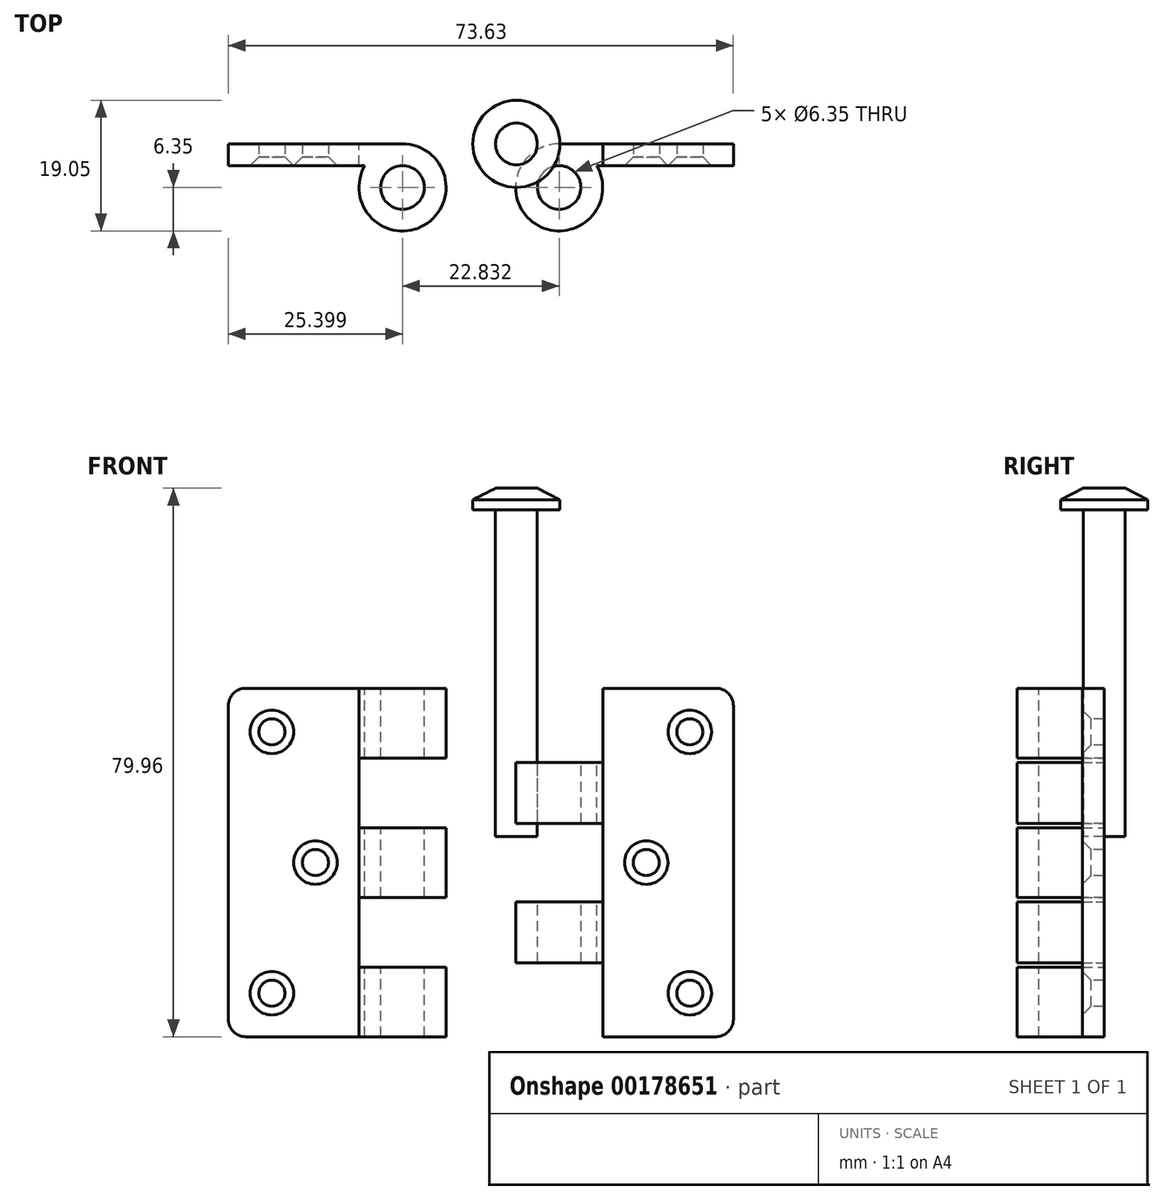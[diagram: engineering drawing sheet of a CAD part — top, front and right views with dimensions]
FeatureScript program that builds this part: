
annotation { "Feature Type Name" : "Feature", "Feature Type Description" : "" }
export const myFeature = defineFeature(function(context is Context, id is Id, definition is map)
    precondition{}
    {
        {
            var Q0;
            Q0=qCreatedBy(makeId("Front.planeOp"),FACE);
            var sketch = newSketch(context, id + "F0", { "sketchPlane" : qUnion([Q0])});
            skLineSegment(sketch, "E0.bottom", {"start": v(-44.61, 38.03) * mm, "end": v(-19.21, 38.03) * mm});
            skLineSegment(sketch, "E0.top", {"start": v(-44.61, -12.77) * mm, "end": v(-19.21, -12.77) * mm});
            skLineSegment(sketch, "E0.left", {"start": v(-44.61, 38.03) * mm, "end": v(-44.61, -12.77) * mm});
            skLineSegment(sketch, "E0.right", {"start": v(-19.21, 38.03) * mm, "end": v(-19.21, -12.77) * mm});
            skSolve(sketch);
        }
        {
            var Q0;
            Q0=qSketchRegion(id+"F0",true);
            extrude(context, id + "F1", {"entities" : qUnion([Q0]), "depth" : 3.17 * mm});
        }
        {
            var Q0;
            Q0=makeQuery(id+"F1.opExtrude","SWEPT_FACE",FACE,{"disambiguationData":[OSD([sQuery(id+"F0.wireOp",EDGE,"E0.bottom")])]});
            var sketch = newSketch(context, id + "F2", { "sketchPlane" : qUnion([Q0])});
            skCircle(sketch, "E1", {"center": v(-19.21, -6.35) * mm, "radius": 6.35 * mm});
            skCircle(sketch, "E2", {"center": v(-19.21, -6.35) * mm, "radius": 3.18 * mm});
            skSolve(sketch);
        }
        {
            var Q0;
            {var subQ5=sQuery(id+"F2.wireOp",EDGE,"E2");Q0=makeQuery(id+"F2.imprint","IMPRINT",FACE,{"disambiguationData":[TD([[makeQuery(id+"F2.imprint","IMPRINT",EDGE,{"derivedFrom":subQ5}),-1.0]])]});}
            var Q1;
            {var subQ1=sQuery(id+"F0.wireOp",EDGE,"E0.bottom");var subQ2=makeQuery(id+"F1.opExtrude","SWEPT_EDGE",EDGE,{"disambiguationData":[OSD([subQ1,sQuery(id+"F0.wireOp",EDGE,"E0.right")])]});Q1=makeQuery(id+"F2.imprint","IMPRINT",FACE,{"disambiguationData":[TD([[makeQuery(id+"F2.imprint","IMPRINT",EDGE,{"derivedFrom":subQ2}),1.0]])]});}
            var Q2;
            Q2=makeQuery(id+"F1.opExtrude","SWEPT_FACE",FACE,{"disambiguationData":[OSD([sQuery(id+"F0.wireOp",EDGE,"E0.top")])]});
            extrude(context, id + "F3", {"entities" : qUnion([Q0, Q1]), "operationType" : NewBodyOperationType.ADD, "endBound" : BoundingType.UP_TO_SURFACE, "oppositeDirection" : true, "endBoundEntityFace" : qUnion([Q2]), "depth" : 25.4 * mm});
        }
        {
            var Q0;
            Q0=makeQuery(id+"F1.opExtrude","CAP_FACE",FACE,{"disambiguationData":[OSD([sQuery(id+"F0.wireOp",EDGE,"E0.bottom"),sQuery(id+"F0.wireOp",EDGE,"E0.top"),sQuery(id+"F0.wireOp",EDGE,"E0.left"),sQuery(id+"F0.wireOp",EDGE,"E0.right")])],"isStart":false});
            var sketch = newSketch(context, id + "F4", { "sketchPlane" : qUnion([Q0])});
            skLineSegment(sketch, "E3", {"start": v(-34.66, 38.03) * mm, "end": v(-34.66, -12.77) * mm, "construction": true});
            skLineSegment(sketch, "E4", {"start": v(-24.7, 12.63) * mm, "end": v(-44.61, 12.63) * mm, "construction": true});
            skLineSegment(sketch, "E5", {"start": v(-24.7, -6.42) * mm, "end": v(-44.61, -6.42) * mm, "construction": true});
            skLineSegment(sketch, "E6", {"start": v(-24.7, 31.68) * mm, "end": v(-44.61, 31.68) * mm, "construction": true});
            skPoint(sketch, "E7", {"position": v(-38.26, 31.68) * mm});
            skPoint(sketch, "E8", {"position": v(-31.91, 12.63) * mm});
            skPoint(sketch, "E9", {"position": v(-38.26, -6.42) * mm});
            skSolve(sketch);
        }
        {
            var Q0;
            Q0=makeQuery(id+"F1.opExtrude","SWEPT_EDGE",EDGE,{"disambiguationData":[OSD([sQuery(id+"F0.wireOp",EDGE,"E0.bottom"),sQuery(id+"F0.wireOp",EDGE,"E0.left")])]});
            var Q1;
            Q1=makeQuery(id+"F1.opExtrude","SWEPT_EDGE",EDGE,{"disambiguationData":[OSD([sQuery(id+"F0.wireOp",EDGE,"E0.top"),sQuery(id+"F0.wireOp",EDGE,"E0.left")])]});
            fillet(context, id + "F5", {"entities" : qUnion([Q0, Q1]), "radius" : 2.54 * mm, "tangentPropagation" : true, "allowEdgeOverflow" : false});
        }
        {
            var Q0;
            Q0=makeQuery(id+"F0.imprint","IMPRINT",FACE,{"disambiguationData":[TD([[makeQuery(id+"F0.imprint","IMPRINT",EDGE,{"derivedFrom":sQuery(id+"F0.wireOp",EDGE,"E0.bottom")}),-1.0]])]});
            var sketch = newSketch(context, id + "F6", { "sketchPlane" : qUnion([Q0])});
            skLineSegment(sketch, "E10", {"start": v(-25.56, -2.61) * mm, "end": v(-12.86, -2.61) * mm});
            skLineSegment(sketch, "E11", {"start": v(-12.86, -2.61) * mm, "end": v(-12.86, 7.55) * mm});
            skLineSegment(sketch, "E12", {"start": v(-12.86, 7.55) * mm, "end": v(-25.56, 7.55) * mm});
            skLineSegment(sketch, "E13", {"start": v(-25.56, 7.55) * mm, "end": v(-25.56, -2.61) * mm});
            skLineSegment(sketch, "E14", {"start": v(-25.56, 17.7) * mm, "end": v(-12.86, 17.7) * mm});
            skLineSegment(sketch, "E15", {"start": v(-12.86, 17.7) * mm, "end": v(-12.86, 27.87) * mm});
            skLineSegment(sketch, "E16", {"start": v(-12.86, 27.87) * mm, "end": v(-25.56, 27.87) * mm});
            skLineSegment(sketch, "E17", {"start": v(-25.56, 27.87) * mm, "end": v(-25.56, 17.7) * mm});
            skPoint(sketch, "E18", {"position": v(-19.21, -2.61) * mm});
            skLineSegment(sketch, "E19", {"start": v(-19.21, 27.87) * mm, "end": v(-19.21, 38.03) * mm});
            skLineSegment(sketch, "E20", {"start": v(-19.21, 17.7) * mm, "end": v(-19.21, 7.55) * mm});
            skLineSegment(sketch, "E21", {"start": v(-19.21, -2.61) * mm, "end": v(-19.21, -12.77) * mm});
            skLineSegment(sketch, "E22", {"start": v(-12.86, 17.7) * mm, "end": v(-12.86, 7.55) * mm});
            skLineSegment(sketch, "E23", {"start": v(-25.56, 7.55) * mm, "end": v(-25.56, 17.7) * mm});
            skLineSegment(sketch, "E24", {"start": v(-25.56, 27.87) * mm, "end": v(-25.56, 38.04) * mm});
            skLineSegment(sketch, "E25", {"start": v(-25.56, 38.04) * mm, "end": v(-12.86, 38.03) * mm});
            skLineSegment(sketch, "E26", {"start": v(-12.86, 38.03) * mm, "end": v(-12.86, 27.87) * mm});
            skLineSegment(sketch, "E27", {"start": v(-12.86, -2.61) * mm, "end": v(-12.86, -12.77) * mm});
            skLineSegment(sketch, "E28", {"start": v(-12.86, -12.77) * mm, "end": v(-25.56, -12.77) * mm});
            skLineSegment(sketch, "E29", {"start": v(-25.56, -12.77) * mm, "end": v(-25.56, -2.61) * mm});
            skSolve(sketch);
        }
        {
            var Q0;
            {var subQ0=sQuery(id+"F6.wireOp",EDGE,"E17");Q0=makeQuery(id+"F6.imprint","IMPRINT",FACE,{"disambiguationData":[TD([[makeQuery(id+"F6.imprint","IMPRINT",EDGE,{"derivedFrom":subQ0}),1.0]])]});}
            var Q1;
            {var subQ0=sQuery(id+"F6.wireOp",EDGE,"E15");Q1=makeQuery(id+"F6.imprint","IMPRINT",FACE,{"disambiguationData":[TD([[makeQuery(id+"F6.imprint","IMPRINT",EDGE,{"derivedFrom":subQ0}),1.0]])]});}
            var Q2;
            {var subQ0=sQuery(id+"F6.wireOp",EDGE,"E13");Q2=makeQuery(id+"F6.imprint","IMPRINT",FACE,{"disambiguationData":[TD([[makeQuery(id+"F6.imprint","IMPRINT",EDGE,{"derivedFrom":subQ0}),1.0]])]});}
            var Q3;
            {var subQ0=sQuery(id+"F6.wireOp",EDGE,"E11");Q3=makeQuery(id+"F6.imprint","IMPRINT",FACE,{"disambiguationData":[TD([[makeQuery(id+"F6.imprint","IMPRINT",EDGE,{"derivedFrom":subQ0}),1.0]])]});}
            extrude(context, id + "F7", {"entities" : qUnion([Q0, Q1, Q2, Q3]), "operationType" : NewBodyOperationType.REMOVE, "depth" : 25.4 * mm});
        }
        {
            var Q0;
            Q0=qCreatedBy(makeId("Front.planeOp"),FACE);
            var sketch = newSketch(context, id + "F8", { "sketchPlane" : qUnion([Q0])});
            skLineSegment(sketch, "E30.bottom", {"start": v(3.62, 38.03) * mm, "end": v(29.02, 38.03) * mm});
            skLineSegment(sketch, "E30.top", {"start": v(3.62, -12.77) * mm, "end": v(29.02, -12.77) * mm});
            skLineSegment(sketch, "E30.left", {"start": v(3.62, 38.03) * mm, "end": v(3.62, -12.77) * mm});
            skLineSegment(sketch, "E30.right", {"start": v(29.02, 38.03) * mm, "end": v(29.02, -12.77) * mm});
            skSolve(sketch);
        }
        {
            var Q0;
            Q0=qSketchRegion(id+"F8",true);
            extrude(context, id + "F9", {"entities" : qUnion([Q0]), "depth" : 3.17 * mm});
        }
        {
            var Q0;
            Q0=makeQuery(id+"F9.opExtrude","SWEPT_FACE",FACE,{"disambiguationData":[OSD([sQuery(id+"F8.wireOp",EDGE,"E30.bottom")])]});
            var sketch = newSketch(context, id + "F10", { "sketchPlane" : qUnion([Q0])});
            skCircle(sketch, "E31", {"center": v(3.62, -6.35) * mm, "radius": 6.35 * mm});
            skLineSegment(sketch, "E32", {"start": v(-33.9, -6.35) * mm, "end": v(23.07, -6.35) * mm, "construction": true});
            skCircle(sketch, "E33", {"center": v(3.62, -6.35) * mm, "radius": 3.18 * mm});
            skSolve(sketch);
        }
        {
            var Q0;
            {var subQ5=sQuery(id+"F10.wireOp",EDGE,"E33");Q0=makeQuery(id+"F10.imprint","IMPRINT",FACE,{"disambiguationData":[TD([[makeQuery(id+"F10.imprint","IMPRINT",EDGE,{"derivedFrom":subQ5}),-1.0]])]});}
            var Q1;
            {var subQ1=sQuery(id+"F8.wireOp",EDGE,"E30.bottom");var subQ2=makeQuery(id+"F9.opExtrude","SWEPT_EDGE",EDGE,{"disambiguationData":[OSD([subQ1,sQuery(id+"F8.wireOp",EDGE,"E30.left")])]});Q1=makeQuery(id+"F10.imprint","IMPRINT",FACE,{"disambiguationData":[TD([[makeQuery(id+"F10.imprint","IMPRINT",EDGE,{"derivedFrom":subQ2}),-1.0]])]});}
            var Q2;
            Q2=makeQuery(id+"F9.opExtrude","SWEPT_FACE",FACE,{"disambiguationData":[OSD([sQuery(id+"F8.wireOp",EDGE,"E30.top")])]});
            extrude(context, id + "F11", {"entities" : qUnion([Q0, Q1]), "operationType" : NewBodyOperationType.ADD, "endBound" : BoundingType.UP_TO_SURFACE, "oppositeDirection" : true, "endBoundEntityFace" : qUnion([Q2]), "depth" : 25.4 * mm});
        }
        {
            var Q0;
            Q0=makeQuery(id+"F9.opExtrude","CAP_FACE",FACE,{"disambiguationData":[OSD([sQuery(id+"F8.wireOp",EDGE,"E30.bottom"),sQuery(id+"F8.wireOp",EDGE,"E30.top"),sQuery(id+"F8.wireOp",EDGE,"E30.left"),sQuery(id+"F8.wireOp",EDGE,"E30.right")])],"isStart":true});
            var sketch = newSketch(context, id + "F12", { "sketchPlane" : qUnion([Q0])});
            skLineSegment(sketch, "E34", {"start": v(-9.97, 27.23) * mm, "end": v(2.73, 27.23) * mm});
            skLineSegment(sketch, "E35", {"start": v(2.73, 27.23) * mm, "end": v(2.73, 38.03) * mm});
            skLineSegment(sketch, "E36", {"start": v(2.73, 38.03) * mm, "end": v(-9.97, 38.03) * mm});
            skLineSegment(sketch, "E37", {"start": v(-9.97, 27.23) * mm, "end": v(-9.97, 38.03) * mm});
            skLineSegment(sketch, "E38", {"start": v(-9.97, 27.23) * mm, "end": v(-9.97, -12.77) * mm});
            skLineSegment(sketch, "E39", {"start": v(-9.97, -12.77) * mm, "end": v(2.73, -12.77) * mm});
            skLineSegment(sketch, "E40", {"start": v(2.73, -12.77) * mm, "end": v(2.73, 27.23) * mm});
            skLineSegment(sketch, "E41", {"start": v(2.73, 18.34) * mm, "end": v(-9.97, 18.34) * mm});
            skLineSegment(sketch, "E42", {"start": v(-9.97, 6.91) * mm, "end": v(2.73, 6.91) * mm});
            skLineSegment(sketch, "E43", {"start": v(-9.97, -1.98) * mm, "end": v(2.73, -1.98) * mm});
            skSolve(sketch);
        }
        {
            var Q0;
            {var subQ0=sQuery(id+"F12.wireOp",EDGE,"E35");Q0=makeQuery(id+"F12.imprint","IMPRINT",FACE,{"disambiguationData":[TD([[makeQuery(id+"F12.imprint","IMPRINT",EDGE,{"derivedFrom":subQ0}),1.0]])]});}
            var Q1;
            {var subQ0=sQuery(id+"F12.wireOp",EDGE,"E37");Q1=makeQuery(id+"F12.imprint","IMPRINT",FACE,{"disambiguationData":[TD([[makeQuery(id+"F12.imprint","IMPRINT",EDGE,{"derivedFrom":subQ0}),-1.0]])]});}
            var Q2;
            {var subQ0=sQuery(id+"F12.wireOp",EDGE,"E41");var subQ1=sQuery(id+"F12.wireOp",EDGE,"E38");var subQ2=makeQuery(id+"F12.imprint","INTERSECT",VERTEX,{"derivedFrom":[subQ1,subQ0]});Q2=makeQuery(id+"F12.imprint","IMPRINT",FACE,{"disambiguationData":[TD([[makeQuery(id+"F12.imprint","IMPRINT",EDGE,{"disambiguationData":[TD([[subQ2,-1.0]])],"derivedFrom":subQ1}),1.0]])]});}
            var Q3;
            {var subQ0=sQuery(id+"F12.wireOp",EDGE,"E41");var subQ1=sQuery(id+"F12.wireOp",EDGE,"E40");var subQ2=makeQuery(id+"F12.imprint","INTERSECT",VERTEX,{"derivedFrom":[subQ1,subQ0]});Q3=makeQuery(id+"F12.imprint","IMPRINT",FACE,{"disambiguationData":[TD([[makeQuery(id+"F12.imprint","IMPRINT",EDGE,{"disambiguationData":[TD([[subQ2,1.0]])],"derivedFrom":subQ1}),1.0]])]});}
            var Q4;
            {var subQ0=sQuery(id+"F12.wireOp",EDGE,"E39");var subQ3=sQuery(id+"F12.wireOp",EDGE,"E40");var subQ4=makeQuery(id+"F12.imprint","INTERSECT",VERTEX,{"derivedFrom":[subQ0,subQ3]});Q4=makeQuery(id+"F12.imprint","IMPRINT",FACE,{"disambiguationData":[TD([[makeQuery(id+"F12.imprint","IMPRINT",EDGE,{"disambiguationData":[TD([[subQ4,1.0]])],"derivedFrom":subQ0}),1.0]])]});}
            var Q5;
            {var subQ1=sQuery(id+"F12.wireOp",EDGE,"E38");var subQ3=sQuery(id+"F12.wireOp",EDGE,"E43");var subQ4=makeQuery(id+"F12.imprint","INTERSECT",VERTEX,{"derivedFrom":[subQ1,subQ3]});Q5=makeQuery(id+"F12.imprint","IMPRINT",FACE,{"disambiguationData":[TD([[makeQuery(id+"F12.imprint","IMPRINT",EDGE,{"disambiguationData":[TD([[subQ4,-1.0]])],"derivedFrom":subQ3}),-1.0]])]});}
            extrude(context, id + "F13", {"entities" : qUnion([Q0, Q1, Q2, Q3, Q4, Q5]), "operationType" : NewBodyOperationType.REMOVE, "oppositeDirection" : true, "depth" : 25.4 * mm});
        }
        {
            var Q0;
            Q0=qCreatedBy(makeId("Front.planeOp"),FACE);
            var sketch = newSketch(context, id + "F14", { "sketchPlane" : qUnion([Q0])});
            skLineSegment(sketch, "E44", {"start": v(-5.65, 64.02) * mm, "end": v(-5.65, 16.4) * mm});
            skLineSegment(sketch, "E45", {"start": v(-5.65, 16.4) * mm, "end": v(-2.6, 16.4) * mm});
            skLineSegment(sketch, "E46", {"start": v(-2.6, 16.4) * mm, "end": v(-2.6, 67.2) * mm});
            skLineSegment(sketch, "E47", {"start": v(-2.6, 67.2) * mm, "end": v(-5.65, 67.2) * mm});
            skLineSegment(sketch, "E48", {"start": v(-5.65, 67.2) * mm, "end": v(-8.96, 65.52) * mm});
            skLineSegment(sketch, "E49", {"start": v(-8.96, 65.52) * mm, "end": v(-8.96, 64.02) * mm});
            skLineSegment(sketch, "E50", {"start": v(-8.96, 64.02) * mm, "end": v(-5.65, 64.02) * mm});
            skSolve(sketch);
        }
        {
            var Q0;
            Q0=qSketchRegion(id+"F14",true);
            var Q1;
            Q1=sQuery(id+"F14.wireOp",EDGE,"E46");
            revolve(context, id + "F15", {"entities" : qUnion([Q0]), "axis" : qUnion([Q1]), "revolveType" : RevolveType.FULL});
        }
        {
            var Q0;
            Q0=makeQuery(id+"F9.opExtrude","CAP_FACE",FACE,{"disambiguationData":[OSD([sQuery(id+"F8.wireOp",EDGE,"E30.bottom"),sQuery(id+"F8.wireOp",EDGE,"E30.top"),sQuery(id+"F8.wireOp",EDGE,"E30.left"),sQuery(id+"F8.wireOp",EDGE,"E30.right")])],"isStart":false});
            var sketch = newSketch(context, id + "F16", { "sketchPlane" : qUnion([Q0])});
            skLineSegment(sketch, "E51", {"start": v(19.5, 38.03) * mm, "end": v(19.5, -12.77) * mm, "construction": true});
            skLineSegment(sketch, "E52", {"start": v(9.97, 12.63) * mm, "end": v(29.02, 12.63) * mm, "construction": true});
            skPoint(sketch, "E53", {"position": v(16.32, 12.63) * mm});
            skPoint(sketch, "E54", {"position": v(22.67, 31.68) * mm});
            skPoint(sketch, "E55", {"position": v(22.67, -6.42) * mm});
            skSolve(sketch);
        }
        {
            var Q0;
            Q0=sQuery(id+"F4.wireOp",VERTEX,"E7");
            var Q1;
            Q1=sQuery(id+"F4.wireOp",VERTEX,"E8");
            var Q2;
            Q2=sQuery(id+"F4.wireOp",VERTEX,"E9");
            var Q3;
            Q3=makeQuery(id+"F1.opExtrude","SWEPT_BODY",BODY,{"disambiguationData":[OSD([sQuery(id+"F0.wireOp",EDGE,"E0.bottom"),sQuery(id+"F0.wireOp",EDGE,"E0.top"),sQuery(id+"F0.wireOp",EDGE,"E0.left"),sQuery(id+"F0.wireOp",EDGE,"E0.right")])]});
            hole(context, id + "F17", {"style" : HoleStyle.C_SINK, "endStyle" : HoleEndStyle.THROUGH, "holeDiameter" : 3.8 * mm, "cSinkDiameter" : 6.35 * mm, "cSinkAngle" : 90 * degree, "locations" : qUnion([Q0, Q1, Q2]), "scope" : qUnion([Q3]), "isTappedThrough" : true});
        }
        {
            var Q0;
            Q0=sQuery(id+"F16.wireOp",VERTEX,"E54");
            var Q1;
            Q1=sQuery(id+"F16.wireOp",VERTEX,"E53");
            var Q2;
            Q2=sQuery(id+"F16.wireOp",VERTEX,"E55");
            var Q3;
            Q3=makeQuery(id+"F9.opExtrude","SWEPT_BODY",BODY,{"disambiguationData":[OSD([sQuery(id+"F8.wireOp",EDGE,"E30.bottom"),sQuery(id+"F8.wireOp",EDGE,"E30.top"),sQuery(id+"F8.wireOp",EDGE,"E30.left"),sQuery(id+"F8.wireOp",EDGE,"E30.right")])]});
            hole(context, id + "F18", {"style" : HoleStyle.C_SINK, "endStyle" : HoleEndStyle.THROUGH, "holeDiameter" : 3.8 * mm, "cSinkDiameter" : 6.35 * mm, "cSinkAngle" : 90 * degree, "locations" : qUnion([Q0, Q1, Q2]), "scope" : qUnion([Q3]), "isTappedThrough" : true});
        }
        {
            var Q0;
            Q0=makeQuery(id+"F9.opExtrude","SWEPT_EDGE",EDGE,{"disambiguationData":[OSD([sQuery(id+"F8.wireOp",EDGE,"E30.bottom"),sQuery(id+"F8.wireOp",EDGE,"E30.right")])]});
            var Q1;
            Q1=makeQuery(id+"F9.opExtrude","SWEPT_EDGE",EDGE,{"disambiguationData":[OSD([sQuery(id+"F8.wireOp",EDGE,"E30.top"),sQuery(id+"F8.wireOp",EDGE,"E30.right")])]});
            fillet(context, id + "F19", {"entities" : qUnion([Q0, Q1]), "radius" : 2.54 * mm, "tangentPropagation" : true, "allowEdgeOverflow" : false});
        }
    });
